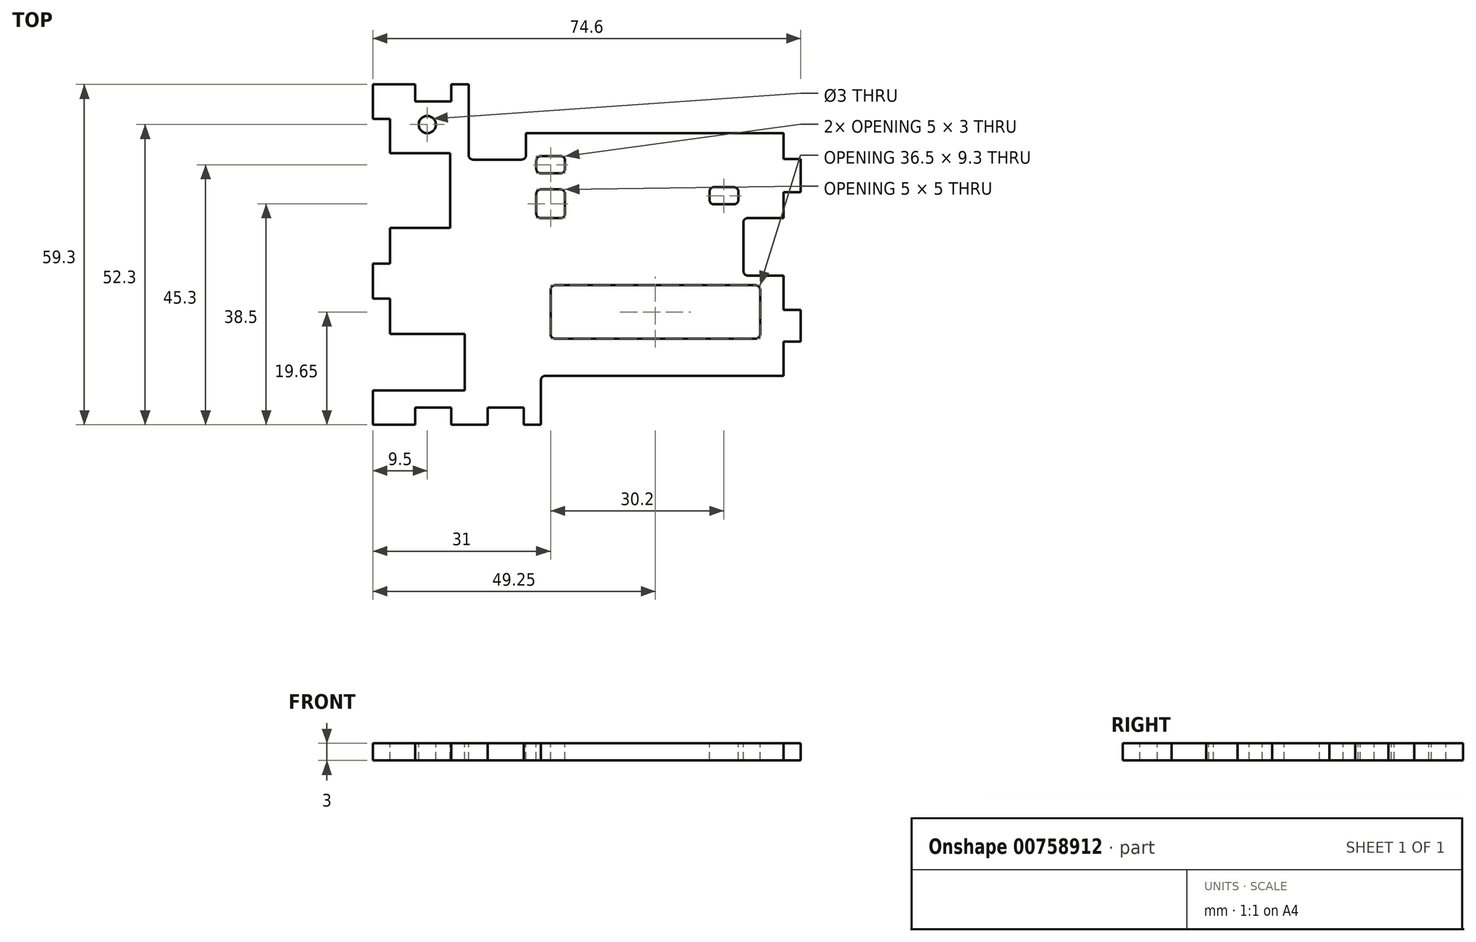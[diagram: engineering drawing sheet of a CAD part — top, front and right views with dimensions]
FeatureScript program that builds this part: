
annotation { "Feature Type Name" : "Feature", "Feature Type Description" : "" }
export const myFeature = defineFeature(function(context is Context, id is Id, definition is map)
    precondition{}
    {
        {
            var Q0;
            Q0=qCreatedBy(makeId("Top.planeOp"),FACE);
            var sketch = newSketch(context, id + "F0", { "sketchPlane" : qUnion([Q0])});
            skLineSegment(sketch, "E0", {"start": v(0, 0) * mm, "end": v(7.4, 0) * mm});
            skLineSegment(sketch, "E1", {"start": v(7.4, 0) * mm, "end": v(7.4, 3) * mm});
            skLineSegment(sketch, "E2", {"start": v(7.4, 3) * mm, "end": v(13.7, 3) * mm});
            skLineSegment(sketch, "E3", {"start": v(13.7, 3) * mm, "end": v(13.7, 0) * mm});
            skLineSegment(sketch, "E4", {"start": v(13.7, 0) * mm, "end": v(20, 0) * mm});
            skLineSegment(sketch, "E5", {"start": v(20, 0) * mm, "end": v(20, 3) * mm});
            skLineSegment(sketch, "E6", {"start": v(20, 3) * mm, "end": v(26.3, 3) * mm});
            skLineSegment(sketch, "E7", {"start": v(26.3, 3) * mm, "end": v(26.3, 0) * mm});
            skLineSegment(sketch, "E8", {"start": v(26.3, 0) * mm, "end": v(29.3, 0) * mm});
            skLineSegment(sketch, "E9", {"start": v(29.3, 0) * mm, "end": v(29.3, 7.75) * mm});
            skLineSegment(sketch, "E10", {"start": v(30.05, 8.5) * mm, "end": v(71.6, 8.5) * mm});
            skLineSegment(sketch, "E11", {"start": v(71.6, 8.5) * mm, "end": v(71.6, 14.5) * mm});
            skLineSegment(sketch, "E12", {"start": v(71.6, 14.5) * mm, "end": v(74.6, 14.5) * mm});
            skLineSegment(sketch, "E13", {"start": v(74.6, 14.5) * mm, "end": v(74.6, 20) * mm});
            skLineSegment(sketch, "E14", {"start": v(74.6, 20) * mm, "end": v(71.6, 20) * mm});
            skLineSegment(sketch, "E15", {"start": v(71.6, 20) * mm, "end": v(71.6, 26) * mm});
            skLineSegment(sketch, "E16", {"start": v(71.6, 26) * mm, "end": v(65.35, 26) * mm});
            skLineSegment(sketch, "E17", {"start": v(64.6, 26.75) * mm, "end": v(64.6, 35.25) * mm});
            skLineSegment(sketch, "E18", {"start": v(65.35, 36) * mm, "end": v(71.6, 36) * mm});
            skLineSegment(sketch, "E19", {"start": v(71.6, 36) * mm, "end": v(71.6, 40.5) * mm});
            skLineSegment(sketch, "E20", {"start": v(71.6, 40.5) * mm, "end": v(74.6, 40.5) * mm});
            skLineSegment(sketch, "E21", {"start": v(74.6, 40.5) * mm, "end": v(74.6, 46.3) * mm});
            skLineSegment(sketch, "E22", {"start": v(74.6, 46.3) * mm, "end": v(71.6, 46.3) * mm});
            skLineSegment(sketch, "E23", {"start": v(71.6, 46.3) * mm, "end": v(71.6, 50.8) * mm});
            skLineSegment(sketch, "E24", {"start": v(71.6, 50.8) * mm, "end": v(26.7, 50.8) * mm});
            skLineSegment(sketch, "E25", {"start": v(26.7, 50.8) * mm, "end": v(26.7, 46.95) * mm});
            skLineSegment(sketch, "E26", {"start": v(25.95, 46.2) * mm, "end": v(17.45, 46.2) * mm});
            skLineSegment(sketch, "E27", {"start": v(16.7, 46.95) * mm, "end": v(16.7, 59.3) * mm});
            skLineSegment(sketch, "E28", {"start": v(16.7, 59.3) * mm, "end": v(13.7, 59.3) * mm});
            skLineSegment(sketch, "E29", {"start": v(13.7, 59.3) * mm, "end": v(13.7, 56.3) * mm});
            skLineSegment(sketch, "E30", {"start": v(13.7, 56.3) * mm, "end": v(7.4, 56.3) * mm});
            skLineSegment(sketch, "E31", {"start": v(7.4, 56.3) * mm, "end": v(7.4, 59.3) * mm});
            skLineSegment(sketch, "E32", {"start": v(7.4, 59.3) * mm, "end": v(0, 59.3) * mm});
            skLineSegment(sketch, "E33", {"start": v(0, 59.3) * mm, "end": v(0, 53.3) * mm});
            skLineSegment(sketch, "E34", {"start": v(0, 53.3) * mm, "end": v(3, 53.3) * mm});
            skLineSegment(sketch, "E35", {"start": v(3, 53.3) * mm, "end": v(3, 47.3) * mm});
            skLineSegment(sketch, "E36", {"start": v(3, 47.3) * mm, "end": v(13.5, 47.3) * mm});
            skLineSegment(sketch, "E37", {"start": v(13.5, 47.3) * mm, "end": v(13.5, 34.3) * mm});
            skLineSegment(sketch, "E38", {"start": v(13.5, 34.3) * mm, "end": v(3, 34.3) * mm});
            skLineSegment(sketch, "E39", {"start": v(3, 34.3) * mm, "end": v(3, 28.1) * mm});
            skLineSegment(sketch, "E40", {"start": v(3, 28.1) * mm, "end": v(0, 28.1) * mm});
            skLineSegment(sketch, "E41", {"start": v(0, 28.1) * mm, "end": v(0, 22) * mm});
            skLineSegment(sketch, "E42", {"start": v(0, 22) * mm, "end": v(3, 22) * mm});
            skLineSegment(sketch, "E43", {"start": v(3, 22) * mm, "end": v(3, 15.8) * mm});
            skLineSegment(sketch, "E44", {"start": v(3, 15.8) * mm, "end": v(16, 15.8) * mm});
            skLineSegment(sketch, "E45", {"start": v(16, 15.8) * mm, "end": v(16, 6) * mm});
            skLineSegment(sketch, "E46", {"start": v(16, 6) * mm, "end": v(0, 6) * mm});
            skLineSegment(sketch, "E47", {"start": v(0, 6) * mm, "end": v(0, 0) * mm});
            skLineSegment(sketch, "E48", {"start": v(31.75, 15) * mm, "end": v(66.75, 15) * mm});
            skLineSegment(sketch, "E49", {"start": v(31, 15.75) * mm, "end": v(31, 23.55) * mm});
            skLineSegment(sketch, "E50", {"start": v(31.75, 24.3) * mm, "end": v(66.75, 24.3) * mm});
            skLineSegment(sketch, "E51", {"start": v(67.5, 23.55) * mm, "end": v(67.5, 15.75) * mm});
            skPoint(sketch, "E52.visualSharp", {"position": v(31, 15) * mm});
            skArc(sketch, "E52.filletArc", {"start": v(31, 15.75) * mm, "mid": v(31.22, 15.22) * mm, "end": v(31.75, 15) * mm});
            skPoint(sketch, "E53.visualSharp", {"position": v(31, 24.3) * mm});
            skArc(sketch, "E53.filletArc", {"start": v(31.75, 24.3) * mm, "mid": v(31.22, 24.08) * mm, "end": v(31, 23.55) * mm});
            skPoint(sketch, "E54.visualSharp", {"position": v(67.5, 24.3) * mm});
            skArc(sketch, "E54.filletArc", {"start": v(67.5, 23.55) * mm, "mid": v(67.28, 24.08) * mm, "end": v(66.75, 24.3) * mm});
            skPoint(sketch, "E55.visualSharp", {"position": v(67.5, 15) * mm});
            skArc(sketch, "E55.filletArc", {"start": v(66.75, 15) * mm, "mid": v(67.28, 15.22) * mm, "end": v(67.5, 15.75) * mm});
            skLineSegment(sketch, "E56.bottom", {"start": v(29.25, 36) * mm, "end": v(32.75, 36) * mm});
            skLineSegment(sketch, "E56.top", {"start": v(29.25, 41) * mm, "end": v(32.75, 41) * mm});
            skLineSegment(sketch, "E56.left", {"start": v(28.5, 36.75) * mm, "end": v(28.5, 40.25) * mm});
            skLineSegment(sketch, "E56.right", {"start": v(33.5, 36.75) * mm, "end": v(33.5, 40.25) * mm});
            skLineSegment(sketch, "E57.bottom", {"start": v(29.25, 43.8) * mm, "end": v(32.75, 43.8) * mm});
            skLineSegment(sketch, "E57.top", {"start": v(29.25, 46.8) * mm, "end": v(32.75, 46.8) * mm});
            skLineSegment(sketch, "E57.left", {"start": v(28.5, 44.55) * mm, "end": v(28.5, 46.05) * mm});
            skLineSegment(sketch, "E57.right", {"start": v(33.5, 44.55) * mm, "end": v(33.5, 46.05) * mm});
            skPoint(sketch, "E58.visualSharp", {"position": v(28.5, 36) * mm});
            skArc(sketch, "E58.filletArc", {"start": v(28.5, 36.75) * mm, "mid": v(28.72, 36.22) * mm, "end": v(29.25, 36) * mm});
            skPoint(sketch, "E59.visualSharp", {"position": v(28.5, 41) * mm});
            skArc(sketch, "E59.filletArc", {"start": v(29.25, 41) * mm, "mid": v(28.72, 40.78) * mm, "end": v(28.5, 40.25) * mm});
            skPoint(sketch, "E60.visualSharp", {"position": v(33.5, 41) * mm});
            skArc(sketch, "E60.filletArc", {"start": v(33.5, 40.25) * mm, "mid": v(33.28, 40.78) * mm, "end": v(32.75, 41) * mm});
            skPoint(sketch, "E61.visualSharp", {"position": v(33.5, 36) * mm});
            skArc(sketch, "E61.filletArc", {"start": v(32.75, 36) * mm, "mid": v(33.28, 36.22) * mm, "end": v(33.5, 36.75) * mm});
            skPoint(sketch, "E62.visualSharp", {"position": v(28.5, 43.8) * mm});
            skArc(sketch, "E62.filletArc", {"start": v(28.5, 44.55) * mm, "mid": v(28.72, 44.02) * mm, "end": v(29.25, 43.8) * mm});
            skPoint(sketch, "E63.visualSharp", {"position": v(28.5, 46.8) * mm});
            skArc(sketch, "E63.filletArc", {"start": v(29.25, 46.8) * mm, "mid": v(28.72, 46.58) * mm, "end": v(28.5, 46.05) * mm});
            skPoint(sketch, "E64.visualSharp", {"position": v(33.5, 46.8) * mm});
            skArc(sketch, "E64.filletArc", {"start": v(33.5, 46.05) * mm, "mid": v(33.28, 46.58) * mm, "end": v(32.75, 46.8) * mm});
            skPoint(sketch, "E65.visualSharp", {"position": v(33.5, 43.8) * mm});
            skArc(sketch, "E65.filletArc", {"start": v(32.75, 43.8) * mm, "mid": v(33.28, 44.02) * mm, "end": v(33.5, 44.55) * mm});
            skLineSegment(sketch, "E66.bottom", {"start": v(59.45, 38.4) * mm, "end": v(62.95, 38.4) * mm});
            skLineSegment(sketch, "E66.top", {"start": v(59.45, 41.4) * mm, "end": v(62.95, 41.4) * mm});
            skLineSegment(sketch, "E66.left", {"start": v(58.7, 39.15) * mm, "end": v(58.7, 40.65) * mm});
            skLineSegment(sketch, "E66.right", {"start": v(63.7, 39.15) * mm, "end": v(63.7, 40.65) * mm});
            skPoint(sketch, "E67.visualSharp", {"position": v(58.7, 41.4) * mm});
            skArc(sketch, "E67.filletArc", {"start": v(59.45, 41.4) * mm, "mid": v(58.92, 41.18) * mm, "end": v(58.7, 40.65) * mm});
            skPoint(sketch, "E68.visualSharp", {"position": v(63.7, 41.4) * mm});
            skArc(sketch, "E68.filletArc", {"start": v(63.7, 40.65) * mm, "mid": v(63.48, 41.18) * mm, "end": v(62.95, 41.4) * mm});
            skPoint(sketch, "E69.visualSharp", {"position": v(63.7, 38.4) * mm});
            skArc(sketch, "E69.filletArc", {"start": v(62.95, 38.4) * mm, "mid": v(63.48, 38.62) * mm, "end": v(63.7, 39.15) * mm});
            skPoint(sketch, "E70.visualSharp", {"position": v(58.7, 38.4) * mm});
            skArc(sketch, "E70.filletArc", {"start": v(58.7, 39.15) * mm, "mid": v(58.92, 38.62) * mm, "end": v(59.45, 38.4) * mm});
            skCircle(sketch, "E71", {"center": v(9.5, 52.3) * mm, "radius": 1.5 * mm});
            skPoint(sketch, "E72.visualSharp", {"position": v(16.7, 46.2) * mm});
            skArc(sketch, "E72.filletArc", {"start": v(16.7, 46.95) * mm, "mid": v(16.92, 46.42) * mm, "end": v(17.45, 46.2) * mm});
            skPoint(sketch, "E73.visualSharp", {"position": v(26.7, 46.2) * mm});
            skArc(sketch, "E73.filletArc", {"start": v(25.95, 46.2) * mm, "mid": v(26.48, 46.42) * mm, "end": v(26.7, 46.95) * mm});
            skPoint(sketch, "E74.visualSharp", {"position": v(64.6, 36) * mm});
            skArc(sketch, "E74.filletArc", {"start": v(65.35, 36) * mm, "mid": v(64.82, 35.78) * mm, "end": v(64.6, 35.25) * mm});
            skPoint(sketch, "E75.visualSharp", {"position": v(64.6, 26) * mm});
            skArc(sketch, "E75.filletArc", {"start": v(64.6, 26.75) * mm, "mid": v(64.82, 26.22) * mm, "end": v(65.35, 26) * mm});
            skPoint(sketch, "E76.visualSharp", {"position": v(29.3, 8.5) * mm});
            skArc(sketch, "E76.filletArc", {"start": v(30.05, 8.5) * mm, "mid": v(29.52, 8.28) * mm, "end": v(29.3, 7.75) * mm});
            skSolve(sketch);
        }
        {
            var Q0;
            Q0=makeQuery(id+"F0.imprint","IMPRINT",FACE,{"disambiguationData":[TD([[makeQuery(id+"F0.imprint","IMPRINT",EDGE,{"derivedFrom":sQuery(id+"F0.wireOp",EDGE,"E0")}),1.0]])]});
            extrude(context, id + "F1", {"entities" : qUnion([Q0]), "oppositeDirection" : true, "depth" : 3 * mm, "offsetDistance" : 25 * mm});
        }
    });
